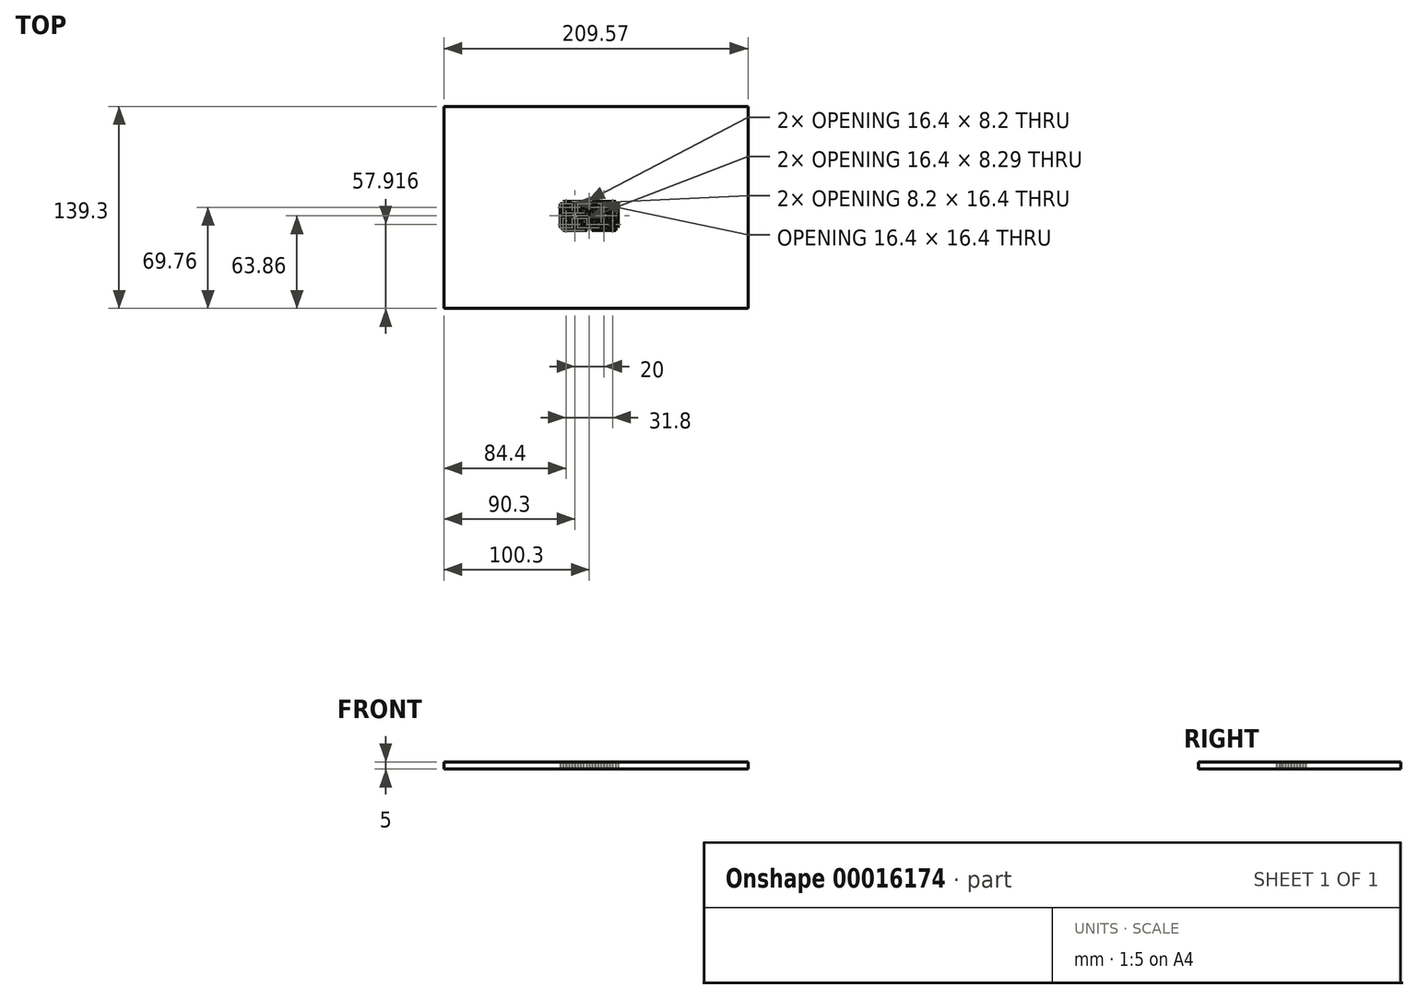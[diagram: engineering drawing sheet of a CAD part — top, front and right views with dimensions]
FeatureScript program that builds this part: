
annotation { "Feature Type Name" : "Feature", "Feature Type Description" : "" }
export const myFeature = defineFeature(function(context is Context, id is Id, definition is map)
    precondition{}
    {
        {
            var Q0;
            Q0=qCreatedBy(makeId("Top.planeOp"),FACE);
            var sketch = newSketch(context, id + "F0", { "sketchPlane" : qUnion([Q0])});
            skLineSegment(sketch, "E0", {"start": v(-125.38, 70.48) * mm, "end": v(-132.98, 70.48) * mm, "construction": true});
            skLineSegment(sketch, "E1", {"start": v(-124.98, 70.88) * mm, "end": v(-124.98, 62.48) * mm, "construction": true});
            skLineSegment(sketch, "E2", {"start": v(-141.38, 66.88) * mm, "end": v(-136.98, 66.88) * mm, "construction": true});
            skLineSegment(sketch, "E3", {"start": v(-141.38, 70.48) * mm, "end": v(-141.38, 78.88) * mm, "construction": true});
            skLineSegment(sketch, "E4", {"start": v(-124.98, 78.88) * mm, "end": v(-124.98, 74.48) * mm, "construction": true});
            skLineSegment(sketch, "E5", {"start": v(-133.38, 62.85) * mm, "end": v(-133.38, 70.48) * mm, "construction": true});
            skLineSegment(sketch, "E6", {"start": v(-129.38, 62.48) * mm, "end": v(-129.38, 66.88) * mm, "construction": true});
            skLineSegment(sketch, "E7", {"start": v(-140.98, 66.48) * mm, "end": v(-140.98, 62.85) * mm, "construction": true});
            skLineSegment(sketch, "E8", {"start": v(-129.38, 74.88) * mm, "end": v(-125.38, 74.88) * mm, "construction": true});
            skLineSegment(sketch, "E9", {"start": v(-125.38, 62.88) * mm, "end": v(-125.38, 70.48) * mm, "construction": true});
            skLineSegment(sketch, "E10", {"start": v(-125.38, 74.88) * mm, "end": v(-125.38, 78.48) * mm, "construction": true});
            skLineSegment(sketch, "E11", {"start": v(-140.98, 78.48) * mm, "end": v(-140.98, 70.88) * mm, "construction": true});
            skLineSegment(sketch, "E12", {"start": v(-140.98, 62.85) * mm, "end": v(-133.38, 62.85) * mm, "construction": true});
            skLineSegment(sketch, "E13", {"start": v(-132.98, 70.88) * mm, "end": v(-124.98, 70.88) * mm, "construction": true});
            skLineSegment(sketch, "E14", {"start": v(-133.38, 70.88) * mm, "end": v(-133.38, 78.88) * mm, "construction": true});
            skLineSegment(sketch, "E15", {"start": v(-141.38, 78.88) * mm, "end": v(-136.98, 78.88) * mm, "construction": true});
            skLineSegment(sketch, "E16", {"start": v(-132.98, 70.48) * mm, "end": v(-132.98, 62.48) * mm, "construction": true});
            skLineSegment(sketch, "E17", {"start": v(-124.98, 62.48) * mm, "end": v(-129.38, 62.48) * mm, "construction": true});
            skLineSegment(sketch, "E18", {"start": v(-132.98, 78.48) * mm, "end": v(-132.98, 70.88) * mm, "construction": true});
            skLineSegment(sketch, "E19", {"start": v(-125.38, 78.48) * mm, "end": v(-132.98, 78.48) * mm, "construction": true});
            skLineSegment(sketch, "E20", {"start": v(-128.98, 66.88) * mm, "end": v(-128.98, 62.88) * mm, "construction": true});
            skLineSegment(sketch, "E21", {"start": v(-136.98, 78.88) * mm, "end": v(-136.98, 74.48) * mm, "construction": true});
            skLineSegment(sketch, "E22", {"start": v(-137.38, 78.48) * mm, "end": v(-140.98, 78.48) * mm, "construction": true});
            skLineSegment(sketch, "E23", {"start": v(-128.98, 62.88) * mm, "end": v(-125.38, 62.88) * mm, "construction": true});
            skLineSegment(sketch, "E24", {"start": v(-140.98, 70.88) * mm, "end": v(-133.38, 70.88) * mm, "construction": true});
            skLineSegment(sketch, "E25", {"start": v(-137.38, 74.48) * mm, "end": v(-137.38, 78.48) * mm, "construction": true});
            skLineSegment(sketch, "E26", {"start": v(-132.98, 62.48) * mm, "end": v(-141.38, 62.48) * mm, "construction": true});
            skLineSegment(sketch, "E27", {"start": v(-136.98, 66.48) * mm, "end": v(-140.98, 66.48) * mm, "construction": true});
            skLineSegment(sketch, "E28", {"start": v(-133.38, 70.48) * mm, "end": v(-141.38, 70.48) * mm, "construction": true});
            skLineSegment(sketch, "E29", {"start": v(-141.38, 62.48) * mm, "end": v(-141.38, 66.88) * mm, "construction": true});
            skLineSegment(sketch, "E30", {"start": v(-133.38, 78.88) * mm, "end": v(-124.98, 78.88) * mm, "construction": true});
            skLineSegment(sketch, "E31", {"start": v(-124.98, 74.48) * mm, "end": v(-129.38, 74.48) * mm, "construction": true});
            skLineSegment(sketch, "E32", {"start": v(-136.98, 74.48) * mm, "end": v(-137.38, 74.48) * mm, "construction": true});
            skLineSegment(sketch, "E33", {"start": v(-129.38, 66.88) * mm, "end": v(-128.98, 66.88) * mm, "construction": true});
            skLineSegment(sketch, "E34", {"start": v(-136.98, 66.88) * mm, "end": v(-136.98, 66.48) * mm, "construction": true});
            skLineSegment(sketch, "E35", {"start": v(-129.38, 74.48) * mm, "end": v(-129.38, 74.88) * mm, "construction": true});
            skLineSegment(sketch, "E36", {"start": v(-2.4, -0.2) * mm, "end": v(-10, -0.2) * mm});
            skLineSegment(sketch, "E37", {"start": v(5.6, 7.8) * mm, "end": v(2, 7.8) * mm});
            skLineSegment(sketch, "E38", {"start": v(-10, -0.2) * mm, "end": v(-10, -8.2) * mm});
            skLineSegment(sketch, "E39", {"start": v(-6, -7.8) * mm, "end": v(-2.4, -7.8) * mm});
            skLineSegment(sketch, "E40", {"start": v(9.8, -8.2) * mm, "end": v(1.6, -8.2) * mm});
            skLineSegment(sketch, "E41", {"start": v(-8, 5.8) * mm, "end": v(-8, 2.2) * mm});
            skLineSegment(sketch, "E42", {"start": v(-4.4, -2.29) * mm, "end": v(-8, -2.29) * mm});
            skLineSegment(sketch, "E43", {"start": v(8, -6.2) * mm, "end": v(3.6, -6.2) * mm});
            skLineSegment(sketch, "E44", {"start": v(7.6, -5.8) * mm, "end": v(7.6, -2.2) * mm});
            skLineSegment(sketch, "E45", {"start": v(-2, 3.8) * mm, "end": v(-6.4, 3.8) * mm});
            skLineSegment(sketch, "E46", {"start": v(1.6, -8.2) * mm, "end": v(1.6, -3.8) * mm});
            skLineSegment(sketch, "E47", {"start": v(-0.4, -1.8) * mm, "end": v(8, -1.8) * mm});
            skLineSegment(sketch, "E48", {"start": v(-2, 0.2) * mm, "end": v(-2, -8.2) * mm});
            skLineSegment(sketch, "E49", {"start": v(-2, -8.2) * mm, "end": v(-6.4, -8.2) * mm});
            skLineSegment(sketch, "E50", {"start": v(-2.4, -7.8) * mm, "end": v(-2.4, -0.2) * mm});
            skLineSegment(sketch, "E51", {"start": v(2, -4.2) * mm, "end": v(2, -7.8) * mm});
            skLineSegment(sketch, "E52", {"start": v(-8.4, 1.8) * mm, "end": v(-8.4, 6.2) * mm});
            skLineSegment(sketch, "E53", {"start": v(-8.4, 6.2) * mm, "end": v(-4, 6.2) * mm});
            skLineSegment(sketch, "E54", {"start": v(5.6, 3.8) * mm, "end": v(5.6, 7.8) * mm});
            skLineSegment(sketch, "E55", {"start": v(9.6, -0.2) * mm, "end": v(1.6, -0.2) * mm});
            skLineSegment(sketch, "E56", {"start": v(4, 6.2) * mm, "end": v(4, 2.2) * mm});
            skLineSegment(sketch, "E57", {"start": v(-6.4, -8.2) * mm, "end": v(-6.4, -3.8) * mm});
            skLineSegment(sketch, "E58", {"start": v(-10, 0.2) * mm, "end": v(-2, 0.2) * mm});
            skLineSegment(sketch, "E59", {"start": v(-2, 8.2) * mm, "end": v(-2, 3.8) * mm});
            skLineSegment(sketch, "E60", {"start": v(-8, -9.8) * mm, "end": v(-0.4, -9.8) * mm});
            skLineSegment(sketch, "E61", {"start": v(6, -4.2) * mm, "end": v(2, -4.2) * mm});
            skLineSegment(sketch, "E62", {"start": v(4, 2.2) * mm, "end": v(7.6, 2.2) * mm});
            skLineSegment(sketch, "E63", {"start": v(-8.4, -10.09) * mm, "end": v(-8.4, -1.89) * mm});
            skLineSegment(sketch, "E64", {"start": v(-0.4, 2.2) * mm, "end": v(-0.4, 9.8) * mm});
            skLineSegment(sketch, "E65", {"start": v(-4.4, -6.29) * mm, "end": v(-4.4, -2.29) * mm});
            skLineSegment(sketch, "E66", {"start": v(9.6, -7.8) * mm, "end": v(9.6, -0.2) * mm});
            skLineSegment(sketch, "E67", {"start": v(-6, -3.8) * mm, "end": v(-6, -7.8) * mm});
            skLineSegment(sketch, "E68", {"start": v(0, 1.8) * mm, "end": v(-8.4, 1.8) * mm});
            skLineSegment(sketch, "E69", {"start": v(2, 0.2) * mm, "end": v(9.6, 0.2) * mm});
            skLineSegment(sketch, "E70", {"start": v(1.6, -3.8) * mm, "end": v(6, -3.8) * mm});
            skLineSegment(sketch, "E71", {"start": v(8, 1.8) * mm, "end": v(3.6, 1.8) * mm});
            skLineSegment(sketch, "E72", {"start": v(2, -7.8) * mm, "end": v(9.6, -7.8) * mm});
            skLineSegment(sketch, "E73", {"start": v(7.6, 9.8) * mm, "end": v(0, 9.8) * mm});
            skLineSegment(sketch, "E74", {"start": v(-8.4, -1.89) * mm, "end": v(-4, -1.89) * mm});
            skLineSegment(sketch, "E75", {"start": v(0, -2.2) * mm, "end": v(0, -9.8) * mm});
            skLineSegment(sketch, "E76", {"start": v(1.6, 8.2) * mm, "end": v(6, 8.2) * mm});
            skLineSegment(sketch, "E77", {"start": v(3.6, -5.8) * mm, "end": v(7.6, -5.8) * mm});
            skLineSegment(sketch, "E78", {"start": v(3.6, 1.8) * mm, "end": v(3.6, 6.2) * mm});
            skLineSegment(sketch, "E79", {"start": v(-8, -2.29) * mm, "end": v(-8, -9.8) * mm});
            skLineSegment(sketch, "E80", {"start": v(-4, -1.89) * mm, "end": v(-4, -6.29) * mm});
            skLineSegment(sketch, "E81", {"start": v(8, -1.8) * mm, "end": v(8, -6.2) * mm});
            skLineSegment(sketch, "E82", {"start": v(7.6, 2.2) * mm, "end": v(7.6, 9.8) * mm});
            skLineSegment(sketch, "E83", {"start": v(1.6, -0.2) * mm, "end": v(1.6, 8.2) * mm});
            skLineSegment(sketch, "E84", {"start": v(-8, 2.2) * mm, "end": v(-0.4, 2.2) * mm});
            skLineSegment(sketch, "E85", {"start": v(7.6, -2.2) * mm, "end": v(0, -2.2) * mm});
            skLineSegment(sketch, "E86", {"start": v(8, 10) * mm, "end": v(8, 1.8) * mm});
            skLineSegment(sketch, "E87", {"start": v(2, 7.8) * mm, "end": v(2, 0.2) * mm});
            skLineSegment(sketch, "E88", {"start": v(0, 9.8) * mm, "end": v(0, 1.8) * mm});
            skLineSegment(sketch, "E89", {"start": v(9.6, 0.2) * mm, "end": v(9.6, 8.2) * mm});
            skLineSegment(sketch, "E90", {"start": v(-10, 7.8) * mm, "end": v(-10, 0.2) * mm});
            skLineSegment(sketch, "E91", {"start": v(-2.4, 7.8) * mm, "end": v(-10, 7.8) * mm});
            skLineSegment(sketch, "E92", {"start": v(-2.4, 4.2) * mm, "end": v(-2.4, 7.8) * mm});
            skLineSegment(sketch, "E93", {"start": v(-0.4, -9.8) * mm, "end": v(-0.4, -1.8) * mm});
            skLineSegment(sketch, "E94", {"start": v(6, 8.2) * mm, "end": v(6, 3.8) * mm});
            skLineSegment(sketch, "E95", {"start": v(0, -9.8) * mm, "end": v(8, -9.8) * mm});
            skLineSegment(sketch, "E96", {"start": v(-4, 5.8) * mm, "end": v(-8, 5.8) * mm});
            skLineSegment(sketch, "E97", {"start": v(-0.4, 9.8) * mm, "end": v(-8.4, 9.8) * mm});
            skLineSegment(sketch, "E98", {"start": v(-6.4, 4.2) * mm, "end": v(-2.4, 4.2) * mm});
            skLineSegment(sketch, "E99", {"start": v(6, 3.8) * mm, "end": v(5.6, 3.8) * mm});
            skLineSegment(sketch, "E100", {"start": v(3.6, 6.2) * mm, "end": v(4, 6.2) * mm});
            skLineSegment(sketch, "E101", {"start": v(6, -3.8) * mm, "end": v(6, -4.2) * mm});
            skLineSegment(sketch, "E102", {"start": v(-6.4, 3.8) * mm, "end": v(-6.4, 4.2) * mm});
            skLineSegment(sketch, "E103", {"start": v(-6.4, -3.8) * mm, "end": v(-6, -3.8) * mm});
            skLineSegment(sketch, "E104", {"start": v(-4, -6.29) * mm, "end": v(-4.4, -6.29) * mm});
            skLineSegment(sketch, "E105", {"start": v(3.6, -6.2) * mm, "end": v(3.6, -5.8) * mm});
            skLineSegment(sketch, "E106", {"start": v(-4, 6.2) * mm, "end": v(-4, 5.8) * mm});
            skLineSegment(sketch, "E107", {"start": v(-2, 8.2) * mm, "end": v(-10.2, 8.2) * mm});
            skLineSegment(sketch, "E108", {"start": v(-10.2, 8.2) * mm, "end": v(-10.2, -8.2) * mm});
            skLineSegment(sketch, "E109", {"start": v(-8.4, -10.09) * mm, "end": v(8, -10.09) * mm});
            skLineSegment(sketch, "E110", {"start": v(9.8, -8.2) * mm, "end": v(9.8, 8.2) * mm});
            skLineSegment(sketch, "E111", {"start": v(8, 10) * mm, "end": v(-8.4, 10) * mm});
            skLineSegment(sketch, "E112", {"start": v(8, -9.8) * mm, "end": v(8, -10.09) * mm});
            skLineSegment(sketch, "E113", {"start": v(9.6, 8.2) * mm, "end": v(9.8, 8.2) * mm});
            skLineSegment(sketch, "E114", {"start": v(-8.4, 9.8) * mm, "end": v(-8.4, 10) * mm});
            skLineSegment(sketch, "E115", {"start": v(-10, -8.2) * mm, "end": v(-10.2, -8.2) * mm});
            skPoint(sketch, "E116.orphan", {"position": v(9.8, 10) * mm});
            skPoint(sketch, "E117.orphan", {"position": v(9.8, -10.09) * mm});
            skPoint(sketch, "E118.orphan", {"position": v(-10.2, -10.09) * mm});
            skPoint(sketch, "E119.start.orphan", {"position": v(-10.2, 10) * mm});
            skLineSegment(sketch, "E120.MirrorCS", {"start": v(28, 9.8) * mm, "end": v(28, 10) * mm});
            skLineSegment(sketch, "E121.MirrorCS", {"start": v(11.6, -9.8) * mm, "end": v(11.6, -10.09) * mm});
            skLineSegment(sketch, "E122.MirrorCS", {"start": v(23.6, 6.2) * mm, "end": v(23.6, 5.8) * mm});
            skLineSegment(sketch, "E123.MirrorCS", {"start": v(16, -6.2) * mm, "end": v(16, -5.8) * mm});
            skLineSegment(sketch, "E124.MirrorCS", {"start": v(23.6, -6.29) * mm, "end": v(24, -6.29) * mm});
            skLineSegment(sketch, "E125.MirrorCS", {"start": v(26, -3.8) * mm, "end": v(25.6, -3.8) * mm});
            skLineSegment(sketch, "E126.MirrorCS", {"start": v(13.6, -3.8) * mm, "end": v(13.6, -4.2) * mm});
            skLineSegment(sketch, "E127.MirrorCS", {"start": v(13.6, 3.8) * mm, "end": v(14, 3.8) * mm});
            skLineSegment(sketch, "E128.MirrorCS", {"start": v(29.6, -8.2) * mm, "end": v(29.8, -8.2) * mm});
            skLineSegment(sketch, "E129.MirrorCS", {"start": v(26, 3.8) * mm, "end": v(26, 4.2) * mm});
            skLineSegment(sketch, "E130.MirrorCS", {"start": v(16, 6.2) * mm, "end": v(15.6, 6.2) * mm});
            skLineSegment(sketch, "E131.MirrorCS", {"start": v(26, 4.2) * mm, "end": v(22, 4.2) * mm});
            skLineSegment(sketch, "E132.MirrorCS", {"start": v(22, -7.8) * mm, "end": v(22, -0.2) * mm});
            skLineSegment(sketch, "E133.MirrorCS", {"start": v(12, 2.2) * mm, "end": v(12, 9.8) * mm});
            skLineSegment(sketch, "E134.MirrorCS", {"start": v(20, 9.8) * mm, "end": v(28, 9.8) * mm});
            skLineSegment(sketch, "E135.MirrorCS", {"start": v(21.6, -8.2) * mm, "end": v(26, -8.2) * mm});
            skLineSegment(sketch, "E136.MirrorCS", {"start": v(24, -6.29) * mm, "end": v(24, -2.29) * mm});
            skLineSegment(sketch, "E137.MirrorCS", {"start": v(11.6, -1.8) * mm, "end": v(11.6, -6.2) * mm});
            skLineSegment(sketch, "E138.MirrorCS", {"start": v(21.6, 0.2) * mm, "end": v(21.6, -8.2) * mm});
            skLineSegment(sketch, "E139.MirrorCS", {"start": v(20, 2.2) * mm, "end": v(20, 9.8) * mm});
            skLineSegment(sketch, "E140.MirrorCS", {"start": v(23.6, -1.89) * mm, "end": v(23.6, -6.29) * mm});
            skLineSegment(sketch, "E141.MirrorCS", {"start": v(23.6, 5.8) * mm, "end": v(27.6, 5.8) * mm});
            skLineSegment(sketch, "E142.MirrorCS", {"start": v(19.6, -9.8) * mm, "end": v(11.6, -9.8) * mm});
            skLineSegment(sketch, "E143.MirrorCS", {"start": v(11.6, 10) * mm, "end": v(28, 10) * mm});
            skLineSegment(sketch, "E144.MirrorCS", {"start": v(20, -1.8) * mm, "end": v(11.6, -1.8) * mm});
            skLineSegment(sketch, "E145.MirrorCS", {"start": v(28, -10.09) * mm, "end": v(28, -1.89) * mm});
            skLineSegment(sketch, "E146.MirrorCS", {"start": v(27.6, -2.29) * mm, "end": v(27.6, -9.8) * mm});
            skLineSegment(sketch, "E147.MirrorCS", {"start": v(13.6, 8.2) * mm, "end": v(13.6, 3.8) * mm});
            skLineSegment(sketch, "E148.MirrorCS", {"start": v(18, -8.2) * mm, "end": v(18, -3.8) * mm});
            skLineSegment(sketch, "E149.MirrorCS", {"start": v(15.6, 2.2) * mm, "end": v(12, 2.2) * mm});
            skLineSegment(sketch, "E150.MirrorCS", {"start": v(16, 1.8) * mm, "end": v(16, 6.2) * mm});
            skLineSegment(sketch, "E151.MirrorCS", {"start": v(18, 8.2) * mm, "end": v(13.6, 8.2) * mm});
            skLineSegment(sketch, "E152.MirrorCS", {"start": v(22, 4.2) * mm, "end": v(22, 7.8) * mm});
            skLineSegment(sketch, "E153.MirrorCS", {"start": v(29.8, 8.2) * mm, "end": v(29.8, -8.2) * mm});
            skLineSegment(sketch, "E154.MirrorCS", {"start": v(12, -5.8) * mm, "end": v(12, -2.2) * mm});
            skLineSegment(sketch, "E155.MirrorCS", {"start": v(27.6, -9.8) * mm, "end": v(20, -9.8) * mm});
            skPoint(sketch, "E156.MirrorP", {"position": v(29.8, 10) * mm});
            skLineSegment(sketch, "E157.MirrorCS", {"start": v(20, -9.8) * mm, "end": v(20, -1.8) * mm});
            skLineSegment(sketch, "E158.MirrorCS", {"start": v(28, -10.09) * mm, "end": v(11.6, -10.09) * mm});
            skLineSegment(sketch, "E159.MirrorCS", {"start": v(21.6, 3.8) * mm, "end": v(26, 3.8) * mm});
            skLineSegment(sketch, "E160.MirrorCS", {"start": v(13.6, -4.2) * mm, "end": v(17.6, -4.2) * mm});
            skLineSegment(sketch, "E161.MirrorCS", {"start": v(16, -5.8) * mm, "end": v(12, -5.8) * mm});
            skLineSegment(sketch, "E162.MirrorCS", {"start": v(19.6, -2.2) * mm, "end": v(19.6, -9.8) * mm});
            skLineSegment(sketch, "E163.MirrorCS", {"start": v(22, 7.8) * mm, "end": v(29.6, 7.8) * mm});
            skLineSegment(sketch, "E164.MirrorCS", {"start": v(21.6, 8.2) * mm, "end": v(29.8, 8.2) * mm});
            skLineSegment(sketch, "E165.MirrorCS", {"start": v(11.6, -6.2) * mm, "end": v(16, -6.2) * mm});
            skLineSegment(sketch, "E166.MirrorCS", {"start": v(21.6, 8.2) * mm, "end": v(21.6, 3.8) * mm});
            skPoint(sketch, "E167.MirrorP", {"position": v(29.8, -10.09) * mm});
            skLineSegment(sketch, "E168.MirrorCS", {"start": v(28, -1.89) * mm, "end": v(23.6, -1.89) * mm});
            skLineSegment(sketch, "E169.MirrorCS", {"start": v(29.6, 7.8) * mm, "end": v(29.6, 0.2) * mm});
            skLineSegment(sketch, "E170.MirrorCS", {"start": v(24, -2.29) * mm, "end": v(27.6, -2.29) * mm});
            skLineSegment(sketch, "E171.MirrorCS", {"start": v(29.6, 0.2) * mm, "end": v(21.6, 0.2) * mm});
            skLineSegment(sketch, "E172.MirrorCS", {"start": v(12, 9.8) * mm, "end": v(19.6, 9.8) * mm});
            skLineSegment(sketch, "E173.MirrorCS", {"start": v(27.6, 5.8) * mm, "end": v(27.6, 2.2) * mm});
            skLineSegment(sketch, "E174.MirrorCS", {"start": v(26, -8.2) * mm, "end": v(26, -3.8) * mm});
            skLineSegment(sketch, "E175.MirrorCS", {"start": v(19.6, 9.8) * mm, "end": v(19.6, 1.8) * mm});
            skLineSegment(sketch, "E176.MirrorCS", {"start": v(15.6, 6.2) * mm, "end": v(15.6, 2.2) * mm});
            skLineSegment(sketch, "E177.MirrorCS", {"start": v(11.6, 1.8) * mm, "end": v(16, 1.8) * mm});
            skLineSegment(sketch, "E178.MirrorCS", {"start": v(17.6, 7.8) * mm, "end": v(17.6, 0.2) * mm});
            skLineSegment(sketch, "E179.MirrorCS", {"start": v(25.6, -7.8) * mm, "end": v(22, -7.8) * mm});
            skLineSegment(sketch, "E180.MirrorCS", {"start": v(29.6, -0.2) * mm, "end": v(29.6, -8.2) * mm});
            skLineSegment(sketch, "E181.MirrorCS", {"start": v(14, 3.8) * mm, "end": v(14, 7.8) * mm});
            skLineSegment(sketch, "E182.MirrorCS", {"start": v(18, -3.8) * mm, "end": v(13.6, -3.8) * mm});
            skLineSegment(sketch, "E183.MirrorCS", {"start": v(11.6, 10) * mm, "end": v(11.6, 1.8) * mm});
            skLineSegment(sketch, "E184.MirrorCS", {"start": v(14, 7.8) * mm, "end": v(17.6, 7.8) * mm});
            skLineSegment(sketch, "E185.MirrorCS", {"start": v(28, 6.2) * mm, "end": v(23.6, 6.2) * mm});
            skLineSegment(sketch, "E186.MirrorCS", {"start": v(12, -2.2) * mm, "end": v(19.6, -2.2) * mm});
            skLineSegment(sketch, "E187.MirrorCS", {"start": v(22, -0.2) * mm, "end": v(29.6, -0.2) * mm});
            skLineSegment(sketch, "E188.MirrorCS", {"start": v(28, 1.8) * mm, "end": v(28, 6.2) * mm});
            skLineSegment(sketch, "E189.MirrorCS", {"start": v(19.6, 1.8) * mm, "end": v(28, 1.8) * mm});
            skLineSegment(sketch, "E190.MirrorCS", {"start": v(27.6, 2.2) * mm, "end": v(20, 2.2) * mm});
            skLineSegment(sketch, "E191.MirrorCS", {"start": v(17.6, -4.2) * mm, "end": v(17.6, -7.8) * mm});
            skLineSegment(sketch, "E192.MirrorCS", {"start": v(25.6, -3.8) * mm, "end": v(25.6, -7.8) * mm});
            skLineSegment(sketch, "E193.MirrorCS", {"start": v(18, -0.2) * mm, "end": v(18, 8.2) * mm});
            skLineSegment(sketch, "E194.MirrorCS", {"start": v(17.6, 0.2) * mm, "end": v(10, 0.2) * mm});
            skLineSegment(sketch, "E195.MirrorCS", {"start": v(10, -0.2) * mm, "end": v(18, -0.2) * mm});
            skLineSegment(sketch, "E196.MirrorCS", {"start": v(10, 0.2) * mm, "end": v(10, 8.2) * mm});
            skLineSegment(sketch, "E197.MirrorCS", {"start": v(10, -7.8) * mm, "end": v(10, -0.2) * mm});
            skLineSegment(sketch, "E198.MirrorCS", {"start": v(9.8, -8.2) * mm, "end": v(18, -8.2) * mm});
            skLineSegment(sketch, "E199.MirrorCS", {"start": v(17.6, -7.8) * mm, "end": v(10, -7.8) * mm});
            skLineSegment(sketch, "E200.MirrorCS", {"start": v(10, 8.2) * mm, "end": v(9.8, 8.2) * mm});
            skSolve(sketch);
        }
        {
            var Q0;
            Q0=qCreatedBy(makeId("Top.planeOp"),FACE);
            var sketch = newSketch(context, id + "F1", { "sketchPlane" : qUnion([Q0])});
            skLineSegment(sketch, "E201.bottom", {"start": v(-90.5, 75.44) * mm, "end": v(119.07, 75.44) * mm});
            skLineSegment(sketch, "E201.top", {"start": v(-90.5, -63.86) * mm, "end": v(119.07, -63.86) * mm});
            skLineSegment(sketch, "E201.left", {"start": v(-90.5, 75.44) * mm, "end": v(-90.5, -63.86) * mm});
            skLineSegment(sketch, "E201.right", {"start": v(119.07, 75.44) * mm, "end": v(119.07, -63.86) * mm});
            skSolve(sketch);
        }
        {
            var Q0;
            Q0=makeQuery(id+"F1.imprint","IMPRINT",FACE,{"disambiguationData":[TD([[makeQuery(id+"F1.imprint","IMPRINT",EDGE,{"derivedFrom":sQuery(id+"F1.wireOp",EDGE,"E201.bottom")}),-1.0]])]});
            extrude(context, id + "F2", {"entities" : qUnion([Q0]), "depth" : 5 * mm});
        }
        {
            var Q0;
            Q0=qSketchRegion(id+"F0",true);
            var Q1;
            Q1=qConstructionFilter(qBodyType(qCreatedBy(id+"F0",EDGE),BodyType.WIRE),ConstructionObject.NO);
            extrude(context, id + "F3", {"entities" : qUnion([Q0]), "operationType" : NewBodyOperationType.REMOVE, "surfaceEntities" : qUnion([Q1]), "depth" : 5 * mm});
        }
    });
